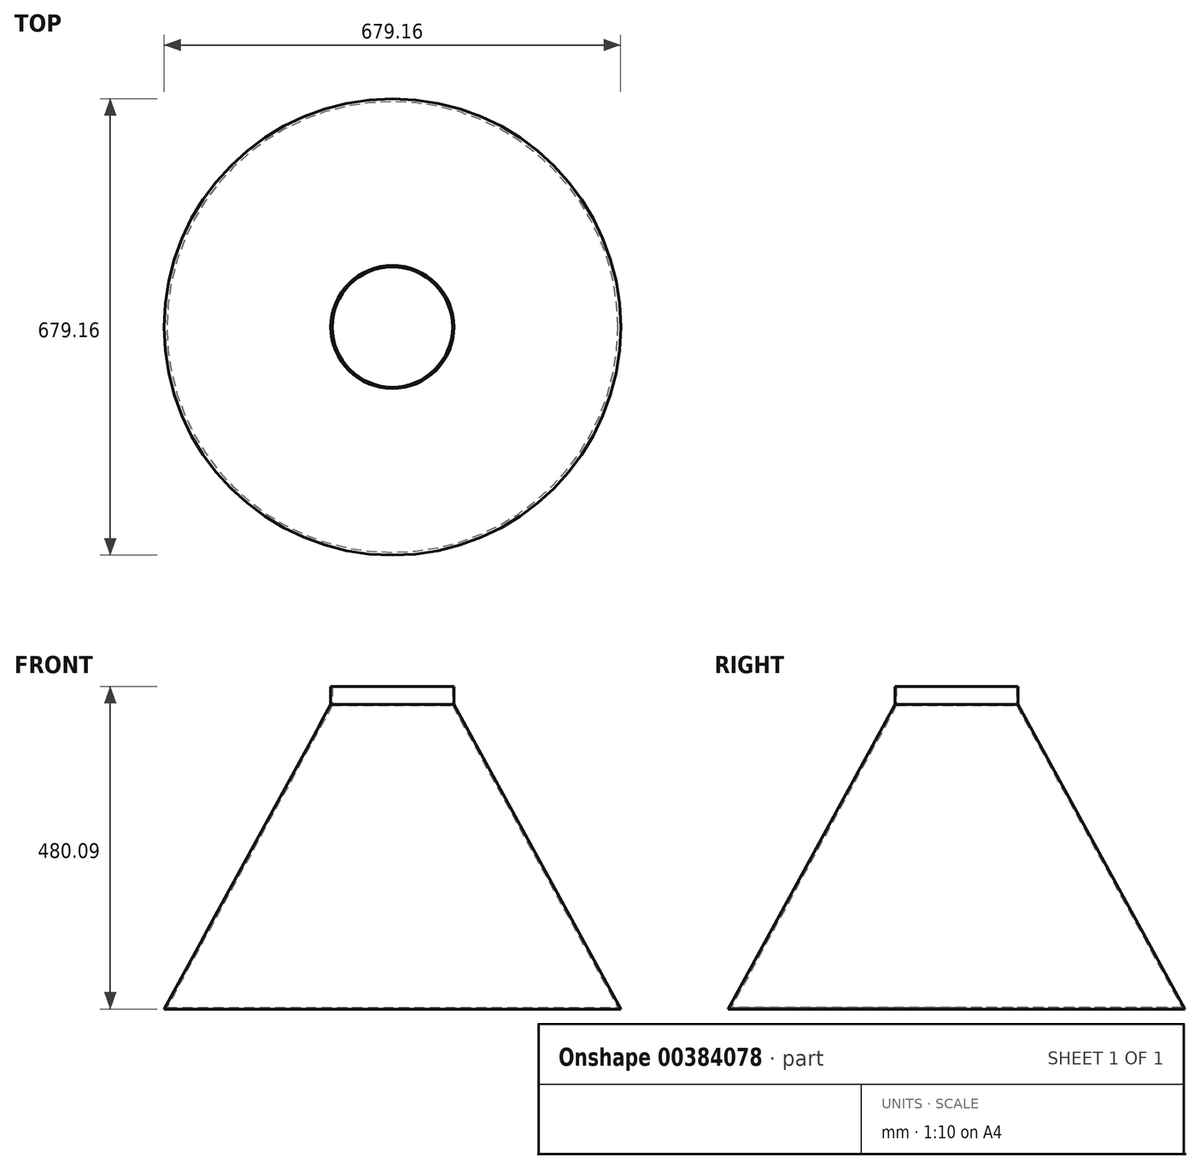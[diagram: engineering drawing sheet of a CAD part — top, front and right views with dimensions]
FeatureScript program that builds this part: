
annotation { "Feature Type Name" : "Feature", "Feature Type Description" : "" }
export const myFeature = defineFeature(function(context is Context, id is Id, definition is map)
    precondition{}
    {
        {
            var Q0;
            Q0=qCreatedBy(makeId("Front.planeOp"),FACE);
            var sketch = newSketch(context, id + "F0", { "sketchPlane" : qUnion([Q0])});
            skLineSegment(sketch, "E0", {"start": v(-264.47, 335.97) * mm, "end": v(-264.47, -539.3) * mm, "construction": true});
            skLineSegment(sketch, "E1", {"start": v(-172.86, 263.45) * mm, "end": v(75.11, -189.64) * mm});
            skLineSegment(sketch, "E2.1", {"start": v(-175.06, 262.19) * mm, "end": v(70.83, -187.1) * mm});
            skLineSegment(sketch, "E3", {"start": v(-264.47, 290.45) * mm, "end": v(-160.39, 290.45) * mm, "construction": true});
            skLineSegment(sketch, "E4", {"start": v(-172.86, 263.45) * mm, "end": v(-172.86, 290.45) * mm});
            skLineSegment(sketch, "E5", {"start": v(-175.06, 262.19) * mm, "end": v(-175.06, 290.45) * mm});
            skLineSegment(sketch, "E6", {"start": v(75.11, -189.64) * mm, "end": v(-264.47, -189.64) * mm, "construction": true});
            skSolve(sketch);
        }
        {
            var Q0;
            Q0=sQuery(id+"F0.wireOp",EDGE,"E2.1");
            var Q1;
            Q1=sQuery(id+"F0.wireOp",EDGE,"E1");
            var Q2;
            Q2=sQuery(id+"F0.wireOp",EDGE,"E5");
            var Q3;
            Q3=sQuery(id+"F0.wireOp",EDGE,"E4");
            var Q4;
            Q4=sQuery(id+"F0.wireOp",EDGE,"E0");
            revolve(context, id + "F1", {"bodyType" : ToolBodyType.SURFACE, "surfaceEntities" : qUnion([Q0, Q1, Q2, Q3]), "axis" : qUnion([Q4]), "revolveType" : RevolveType.FULL});
        }
    });
